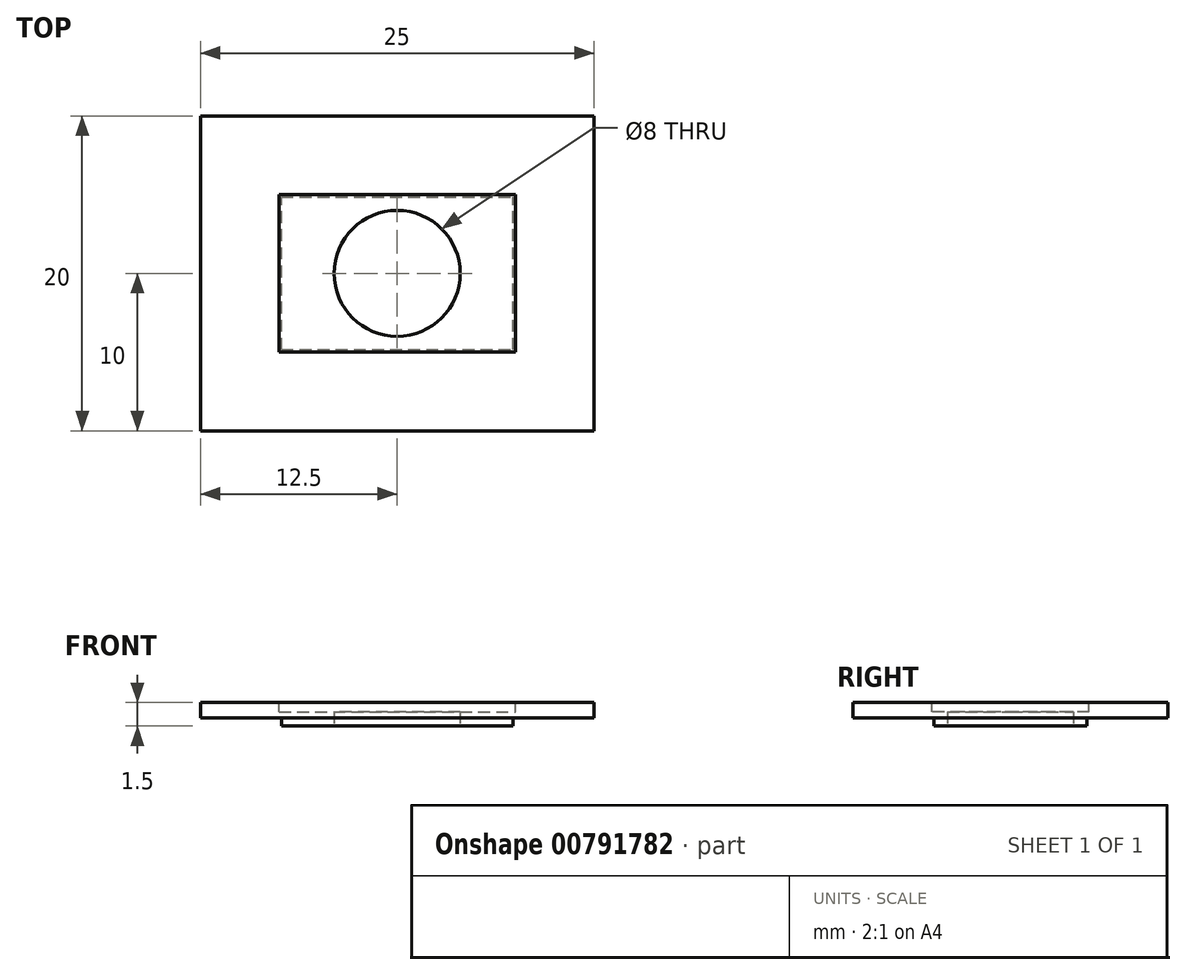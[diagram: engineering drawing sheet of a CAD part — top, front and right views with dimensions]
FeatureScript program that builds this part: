
annotation { "Feature Type Name" : "Feature", "Feature Type Description" : "" }
export const myFeature = defineFeature(function(context is Context, id is Id, definition is map)
    precondition{}
    {
        {
            var Q0;
            Q0=qCreatedBy(makeId("Top.planeOp"),FACE);
            var sketch = newSketch(context, id + "F0", { "sketchPlane" : qUnion([Q0])});
            skLineSegment(sketch, "E0.bottom", {"start": v(-12.5, 10) * mm, "end": v(12.5, 10) * mm});
            skLineSegment(sketch, "E0.top", {"start": v(-12.5, -10) * mm, "end": v(12.5, -10) * mm});
            skLineSegment(sketch, "E0.left", {"start": v(-12.5, 10) * mm, "end": v(-12.5, -10) * mm});
            skLineSegment(sketch, "E0.right", {"start": v(12.5, 10) * mm, "end": v(12.5, -10) * mm});
            skCircle(sketch, "E1", {"center": v(0, 0) * mm, "radius": 4 * mm});
            skSolve(sketch);
        }
        {
            var Q0;
            Q0=qSketchRegion(id+"F0",true);
            extrude(context, id + "F1", {"entities" : qUnion([Q0]), "depth" : 1 * mm, "offsetDistance" : 25 * mm});
        }
        {
            var Q0;
            Q0=makeQuery(id+"F1.opExtrude","CAP_FACE",FACE,{"disambiguationData":[OSD([sQuery(id+"F0.wireOp",EDGE,"E0.bottom"),sQuery(id+"F0.wireOp",EDGE,"E0.top"),sQuery(id+"F0.wireOp",EDGE,"E0.left"),sQuery(id+"F0.wireOp",EDGE,"E0.right"),sQuery(id+"F0.wireOp",EDGE,"E1")])],"isStart":false});
            var sketch = newSketch(context, id + "F2", { "sketchPlane" : qUnion([Q0])});
            skLineSegment(sketch, "E2.bottom", {"start": v(-7.5, 5) * mm, "end": v(7.5, 5) * mm});
            skLineSegment(sketch, "E2.top", {"start": v(-7.5, -5) * mm, "end": v(7.5, -5) * mm});
            skLineSegment(sketch, "E2.left", {"start": v(-7.5, 5) * mm, "end": v(-7.5, -5) * mm});
            skLineSegment(sketch, "E2.right", {"start": v(7.5, 5) * mm, "end": v(7.5, -5) * mm});
            skSolve(sketch);
        }
        {
            var Q0;
            Q0=qSketchRegion(id+"F2",true);
            extrude(context, id + "F3", {"entities" : qUnion([Q0]), "operationType" : NewBodyOperationType.REMOVE, "oppositeDirection" : true, "depth" : 0.6 * mm, "offsetDistance" : 25 * mm});
        }
        {
            var Q0;
            Q0=makeQuery(id+"F1.opExtrude","CAP_FACE",FACE,{"disambiguationData":[OSD([sQuery(id+"F0.wireOp",EDGE,"E0.bottom"),sQuery(id+"F0.wireOp",EDGE,"E0.top"),sQuery(id+"F0.wireOp",EDGE,"E0.left"),sQuery(id+"F0.wireOp",EDGE,"E0.right"),sQuery(id+"F0.wireOp",EDGE,"E1")])],"isStart":true});
            var sketch = newSketch(context, id + "F4", { "sketchPlane" : qUnion([Q0])});
            skLineSegment(sketch, "E3.bottom", {"start": v(-7.35, 4.85) * mm, "end": v(7.35, 4.85) * mm});
            skLineSegment(sketch, "E3.top", {"start": v(-7.35, -4.85) * mm, "end": v(7.35, -4.85) * mm});
            skLineSegment(sketch, "E3.left", {"start": v(-7.35, 4.85) * mm, "end": v(-7.35, -4.85) * mm});
            skLineSegment(sketch, "E3.right", {"start": v(7.35, 4.85) * mm, "end": v(7.35, -4.85) * mm});
            skSolve(sketch);
        }
        {
            var Q0;
            Q0=makeQuery(id+"F4.imprint","IMPRINT",FACE,{"disambiguationData":[TD([[makeQuery(id+"F4.imprint","IMPRINT",EDGE,{"derivedFrom":sQuery(id+"F4.wireOp",EDGE,"E3.bottom")}),-1.0]])]});
            extrude(context, id + "F5", {"entities" : qUnion([Q0]), "operationType" : NewBodyOperationType.ADD, "depth" : 0.5 * mm, "offsetDistance" : 25 * mm});
        }
    });
